# Revit family: axor_showers_thermostatic_bath_mixer_800_45420820
name_source: partatom
category: Plumbing Fixtures
revit_build: Autodesk Revit 2015 (Build: 20140903_1530(x64)
units: mm (PartAtom-declared; Revit-internal decimal feet)

## types (1)
- Brushed Nickel
    BIMobject category = Taps & Mixers
    BOSUseNativeGeometries = 1
    Default Elevation = 4' - 0"
    Design country = Germany
    EAN code = https://4059625011997
    Edition number = 1
    IFC Classification = Sanitary Terminal
    Installation instructions = https://pro.hansgrohe-int.com
    Manufacturer country = Germany
    Manufacturer name = AXOR
    Masterformat 2014 Code = 22 41 39
    Masterformat 2014 Description = Residential Faucets, Supplies, and Trim
    NBS Reference Code = 35-06-07
    NBS Reference Description = Bath Water Supply Fittings
    Nominal height = 0
    Nominal width = 0
    OmniClass Code = 23-31 11 00
    OmniClass Description = Faucets
    Product Guid = 26e10db3-8897-4b1a-92e9-a60853f6680f
    Product SKU = 45420820
    Product data url = https://bimobject.com
    Product family = AXOR Showers
    Product group = Bath thermostat
    Product name = AXOR Showers Thermostatic bath mixer 800 45420820
    Product url = https://pro.hansgrohe-int.com
    QR code = http://bimobject.com
    Technical description = https://pro.hansgrohe-int.com
    UNSPSC Code = 301815
    Uniclass 1.4 Code = L725111
    Uniclass 1.4 Description = Mixer taps
    Uniclass 2.0 Code = PR-35-79-79
    Uniclass 2.0 Description = Sink Water Supply Fittings
    Uniclass 2015 Code = Pr_40_20_87_09
    Uniclass 2015 Name = Bath taps
    Uniformat II Code = D2010
    Uniformat II Description = Plumbing Fixtures
    Weight Net (Kg) = 0

## geometry (parser evidence)
native form markers: Sweep x2
no freeform markers — native parametric forms only
